# Revit family: Access_Door-Acudor-Bauco_Plus-BP-58_Series
name_source: partatom
category: Specialty Equipment
revit_build: Autodesk Revit 2014 (Build: 20130308_1515(x64)
units: mm (PartAtom-declared; Revit-internal decimal feet)

## types (4) — shared parameters
1/2" Drywall = No
5/8" Drywall = Yes
Assembly Code = C1020700
Ceiling Mounted = No
Default Elevation = 48"
Description = Bauco Plus-Drywall Panel Door
Drywall Thickness = 5/8"
Finish = Aluminum Extrusion-Acudor-Mill Finish
Installation Type = Wall Mounted
Length = 25/32"
Manufacturer = Acudor
Material = Aluminum Extrusion-Acudor-Mill Finish
Product Documentation Link = https://www.acudor.com
Product Page URL = https://www.acudor.com
SC - stainless steel screwdriver operated cam latch = No
URL = http://acudor.com
Wall Mounted = Yes

## per-type parameters (varying)
| type | Height | Width |
| BP-58 12x12 | 12" | 12" |
| BP-58 18x18 | 18" | 18" |
| BP-58 24x24 | 24" | 24" |
| BP-58 24x36 | 36" | 24" |

note: column(s) folded — value = type name in every type: Model

## geometry (parser evidence)
native form markers: Extrusion x13, Sweep x1
no freeform markers — native parametric forms only
